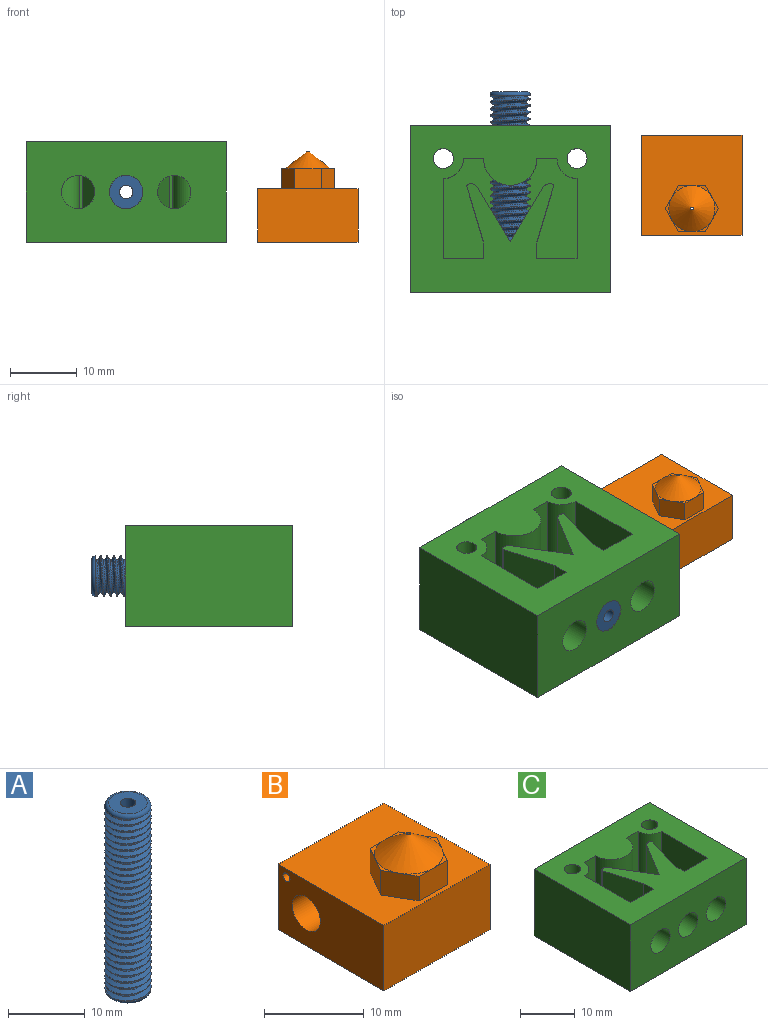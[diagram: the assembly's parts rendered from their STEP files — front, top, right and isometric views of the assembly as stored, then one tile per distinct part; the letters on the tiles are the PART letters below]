
ASSEMBLY  parts=3 mates=1
PART A: 11 faces, bbox 6.8x7.2x30.3 mm
  f0: cylinder r=3mm len=29mm, axis (0,0,-1), area 171.3mm2, adj f3,f4,f6,f7
  f1: plane 5x5mm, normal (0,0,1), area 16.5mm2, adj f4,f10
  f2: plane 5x5mm, normal (0,0,-1), area 16.5mm2, adj f3,f10
  f3: torus R=2.5mm, axis (0,0,1), area 13.9mm2, adj f0,f2,f9
  f4: torus R=2.5mm, axis (0,0,1), area 13.9mm2, adj f0,f1,f8
  f5: bspline ~29.75x5.68mm, area 123.1mm2, adj f6,f7,f8,f9
  f6: bspline ~29.81x6.93mm, area 311.3mm2, adj f0,f5,f8,f9
  f7: bspline ~29.65x6.93mm, area 312.6mm2, adj f0,f5,f8,f9
  f8: plane 6.28x6.28mm, normal (0,0,-1), area 5.5mm2, adj f4,f5,f6,f7
  f9: plane 6.28x6.28mm, normal (0,0,1), area 5.5mm2, adj f3,f5,f6,f7
  f10: cylinder r=1mm len=30mm, axis (0,0,-1), area 188.5mm2, adj f1,f2
PART B: 25 faces, bbox 15x15x13.5 mm
  f0: plane 1x1mm, normal (-1,0,0), area 0.8mm2, adj f7
  f1: plane 3.45x3mm, normal (-0.87,0.5,0), area 12mm2, adj f2,f6,f9,f10,f11
  f2: plane 3.45x3mm, normal (-0.87,-0.5,0), area 12mm2, adj f1,f3,f9,f11,f12
  f3: plane 3.98x3mm, normal (0,-1,0), area 12mm2, adj f2,f4,f9,f12,f13
  f4: plane 3.45x3mm, normal (0.87,-0.5,0), area 12mm2, adj f3,f5,f9,f13,f14
  f5: plane 3.45x3mm, normal (0.87,0.5,0), area 12mm2, adj f4,f6,f9,f14,f15
  f6: plane 3.98x3mm, normal (0,1,0), area 12mm2, adj f1,f5,f9,f10,f15
  f7: cylinder r=0.5mm len=4mm, axis (1,0,0), area 12.6mm2, adj f0,f18
  f8: cylinder r=2mm len=15mm, axis (1,0,0), area 188.5mm2, adj f16,f18
  f9: plane 15x15mm, normal (0,0,1), area 183.8mm2, adj f1,f2,f3,f4,f5,f6,f16,f17
  f10: plane 2.99x1.73mm, normal (0,0,1), area 0.6mm2, adj f1,f6,f20
  f11: plane 3.45x1mm, normal (0,0,1), area 0.6mm2, adj f1,f2,f20
  f12: plane 2.99x1.73mm, normal (0,0,1), area 0.6mm2, adj f2,f3,f20
  f13: plane 2.99x1.73mm, normal (0,0,1), area 0.6mm2, adj f3,f4,f20
  f14: plane 3.45x1mm, normal (0,0,1), area 0.6mm2, adj f4,f5,f20
  f15: plane 2.99x1.73mm, normal (0,0,1), area 0.6mm2, adj f5,f6,f20
  f16: plane 15x8mm, normal (1,0,0), area 107.4mm2, adj f8,f9,f17,f19,f21
  f17: plane 15x8mm, normal (0,1,0), area 120mm2, adj f9,f16,f18,f21
  f18: plane 15x8mm, normal (-1,0,0), area 106.6mm2, adj f7,f8,f9,f17,f19,f21
  f19: plane 15x8mm, normal (0,-1,0), area 120mm2, adj f9,f16,f18,f21
  f20: cone r=1.82mm half-angle=52.4deg, axis (0,0,-1), area 47mm2, adj f10,f11,f12,f13,f14,f15,f22
  f21: plane 15x15mm, normal (0,0,-1), area 217.9mm2, adj f16,f17,f18,f19,f23
  f22: cylinder r=0.2mm len=2.5mm, axis (0,0,-1), area 3.1mm2, adj f20,f24
  f23: cylinder r=1.5mm len=11mm, axis (0,0,1), area 103.7mm2, adj f21,f24
  f24: plane 3x3mm, normal (0,0,-1), area 6.9mm2, adj f22,f23
PART C: 34 faces, bbox 30x25x15 mm
  f0: plane 30x15mm, normal (0,-1,0), area 391.1mm2, adj f1,f3,f27,f28,f29,f30,f31
  f1: plane 25x15mm, normal (1,0,0), area 375mm2, adj f0,f2,f27,f28
  f2: plane 30x15mm, normal (0,1,0), area 430.4mm2, adj f1,f3,f27,f28,f32
  f3: plane 25x15mm, normal (-1,0,0), area 375mm2, adj f0,f2,f27,f28
  f4: plane 14x12mm, normal (1,0,0), area 168mm2, adj f5,f25,f27,f33
  f5: cylinder r=3mm len=14mm, axis (0,0,-1), area 66mm2, adj f4,f6,f27,f33
  f6: plane 14x3mm, normal (0,-1,0), area 42mm2, adj f5,f7,f27,f33
  f7: cylinder r=4mm len=14mm, axis (0,0,-1), area 155.2mm2, adj f6,f8,f27,f32,f33
  f8: plane 14x3mm, normal (0,-1,0), area 42mm2, adj f7,f9,f27,f33
  f9: cylinder r=3mm len=14mm, axis (0,0,-1), area 66mm2, adj f8,f10,f27,f33
  f10: plane 14x12mm, normal (-1,0,0), area 168mm2, adj f9,f11,f27,f33
  f11: plane 14x6mm, normal (0,1,0), area 64.4mm2, adj f10,f12,f27,f31,f33
  f12: plane 14x2.5mm, normal (1,0,0), area 35mm2, adj f11,f13,f27,f33
  f13: plane 14x8.26mm, normal (0.96,-0.29,0), area 120.7mm2, adj f12,f14,f27,f33
  f14: cylinder r=0.31mm len=14mm, axis (0,0,-1), area 6.8mm2, adj f13,f15,f27,f33
  f15: plane 14x0.13mm, normal (0.29,0.96,0), area 1.9mm2, adj f14,f16,f27,f33
  f16: cylinder r=1mm len=14mm, axis (0,0,-1), area 18.4mm2, adj f15,f17,f27,f33
  f17: plane 14x8.24mm, normal (-0.86,0.52,0), area 115.9mm2, adj f16,f18,f27,f30,f33
  f18: plane 14x8.24mm, normal (0.86,0.52,0), area 115.9mm2, adj f17,f19,f27,f30,f33
  f19: cylinder r=1mm len=14mm, axis (0,0,-1), area 18.4mm2, adj f18,f20,f27,f33
  f20: plane 14x0.13mm, normal (-0.29,0.96,0), area 1.9mm2, adj f19,f21,f27,f33
  f21: cylinder r=0.31mm len=14mm, axis (0,0,-1), area 6.8mm2, adj f20,f22,f27,f33
  f22: plane 14x8.26mm, normal (-0.96,-0.29,0), area 120.7mm2, adj f21,f23,f27,f33
  f23: plane 14x2.5mm, normal (-1,0,0), area 35mm2, adj f22,f25,f27,f33
  f24: cylinder r=1.5mm len=15mm, axis (0,0,-1), area 141.4mm2, adj f27,f28
  f25: plane 14x6mm, normal (0,1,0), area 64.4mm2, adj f4,f23,f27,f29,f33
  f26: cylinder r=1.5mm len=15mm, axis (0,0,-1), area 141.4mm2, adj f27,f28
  f27: plane 30x25mm, normal (0,0,1), area 541.3mm2, adj f0,f1,f2,f3,f4,f5,f6,f7
  f28: plane 30x25mm, normal (0,0,-1), area 735.9mm2, adj f0,f1,f2,f3,f24,f26
  f29: cylinder r=2.5mm len=5mm, axis (0,-1,0), area 78.5mm2, adj f0,f25
  f30: cylinder r=2.5mm len=11.64mm, axis (0,-1,0), area 159.1mm2, adj f0,f17,f18
  f31: cylinder r=2.5mm len=5mm, axis (0,-1,0), area 78.5mm2, adj f0,f11
  f32: cylinder r=2.5mm len=9mm, axis (0,-1,0), area 134.7mm2, adj f2,f7
  f33: plane 20x15mm, normal (0,0,1), area 194.5mm2, adj f4,f5,f6,f7,f8,f9,f10,f11
PLACE A rot(axis=(-1,0,0),90deg) t=(-2.52,-13.79,0.25)mm
PLACE B t=(24.68,-1.29,-7.25)mm
PLACE C t=(-2.52,-1.29,-7.25)mm
MATE fastened A.f10 <-> C.f30  axis (0,-1,0) through (-2.52,-13.79,0.25)mm
